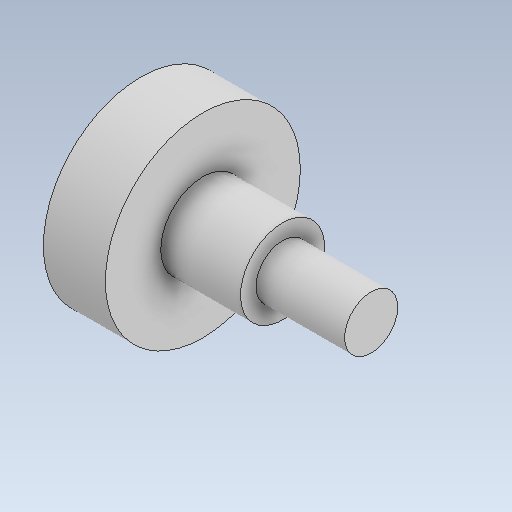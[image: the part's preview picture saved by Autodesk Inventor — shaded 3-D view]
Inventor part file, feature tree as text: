
AUTODESK INVENTOR PART (.ipt)
format: ipt  version: 2020 (Build 240168000, 168)  size: 114,688 bytes
history: native  units: mm
features: other x3, sketch x1
ambient origin geometry x8: Origin, YZ Plane, XZ Plane, XY Plane, X Axis, Y Axis, Z Axis, Center Point
bodies: Solid1 (feature_tree)
feature tree (4):
  other  "guia.ipt"
  other  "Solid1::guia.ipt"
  other  "TaggingFeature1"
  sketch  "Sketch1"  dims[d0=10.0mm]
